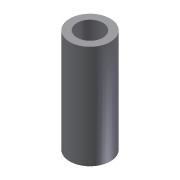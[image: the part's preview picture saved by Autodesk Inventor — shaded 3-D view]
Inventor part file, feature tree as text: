
AUTODESK INVENTOR PART (.ipt)
format: ipt  version: 2012 (Build 160160000, 160)  size: 71,168 bytes
history: native  units: mm
features: extrude x1, sketch x1
ambient origin geometry x8: Origin, YZ Plane, XZ Plane, XY Plane, X Axis, Y Axis, Z Axis, Center Point
bodies: Solid1 (feature_tree)
feature tree (2):
  extrude  "Extrusion1"  Depth=8.0mm
  sketch  "Sketch1"  dims[d0=5.1mm d1=8.0mm d2=20.4mm d3=0.0mm]
